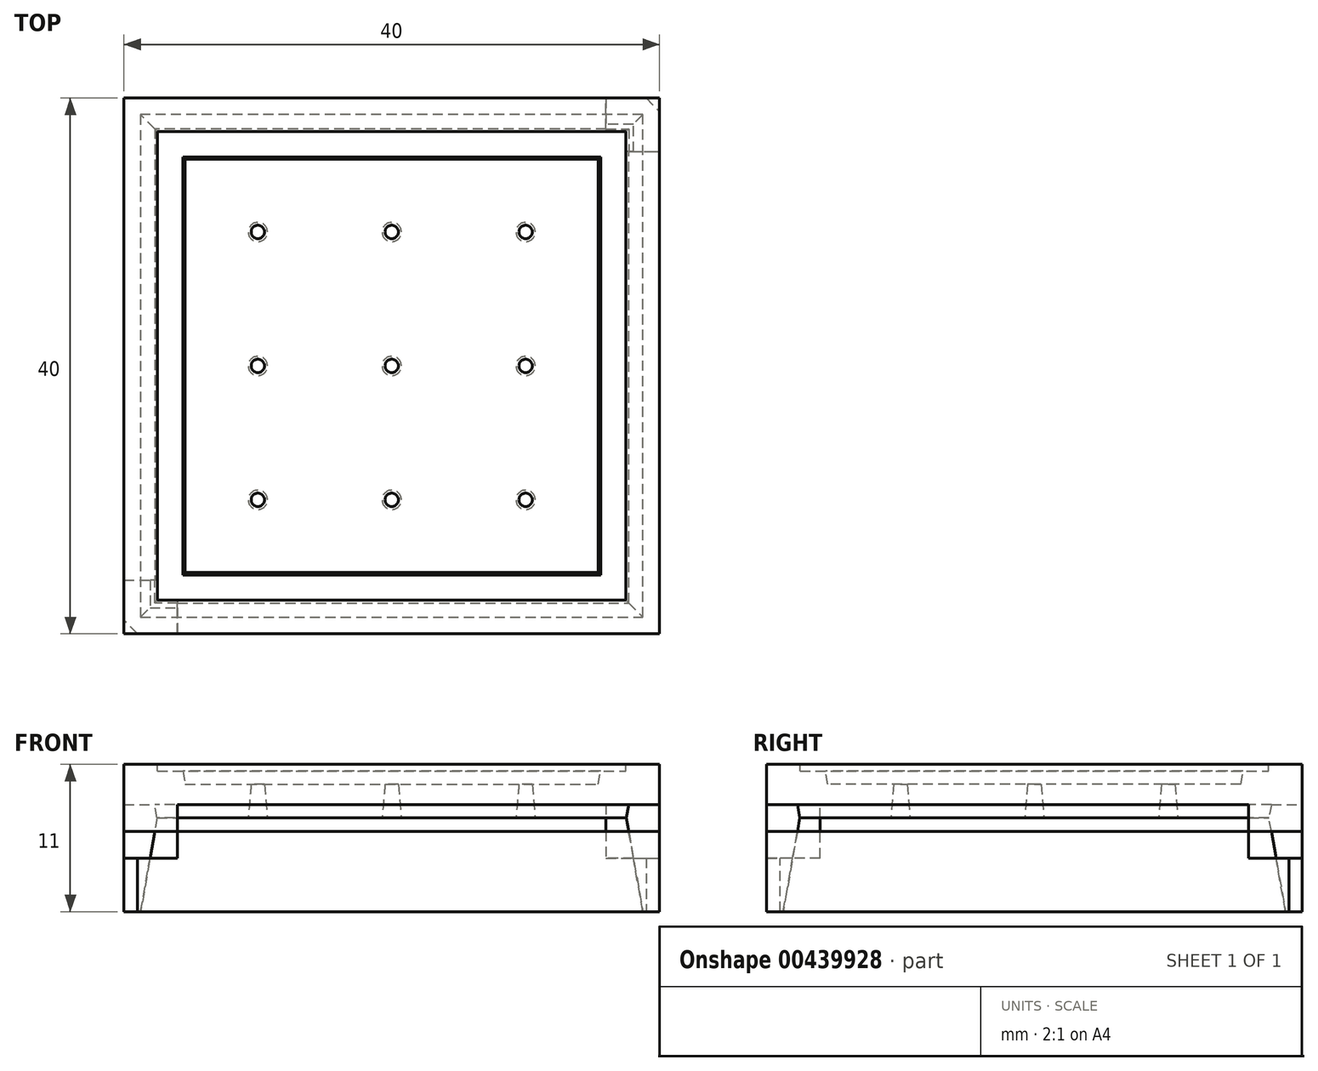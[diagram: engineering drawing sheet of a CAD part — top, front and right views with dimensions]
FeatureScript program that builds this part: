
annotation { "Feature Type Name" : "Feature", "Feature Type Description" : "" }
export const myFeature = defineFeature(function(context is Context, id is Id, definition is map)
    precondition{}
    {
        {
            var Q0;
            Q0=qCreatedBy(makeId("Top.planeOp"),FACE);
            var sketch = newSketch(context, id + "F0", { "sketchPlane" : qUnion([Q0])});
            skLineSegment(sketch, "E0.bottom", {"start": v(0, 0) * mm, "end": v(40, 0) * mm});
            skLineSegment(sketch, "E0.top", {"start": v(0, 40) * mm, "end": v(40, 40) * mm});
            skLineSegment(sketch, "E0.left", {"start": v(0, 0) * mm, "end": v(0, 40) * mm});
            skLineSegment(sketch, "E0.right", {"start": v(40, 0) * mm, "end": v(40, 40) * mm});
            skSolve(sketch);
        }
        {
            var Q0;
            Q0 = qSketchRegion(id + "F0", true);
            extrude(context, id + "F1", {"entities" : qUnion([Q0]), "depth" : 6 * mm});
        }
        {
            var Q0;
            Q0=makeQuery(id+"F1.opExtrude","CAP_FACE",FACE,{"disambiguationData":[OSD([sQuery(id+"F0.wireOp",EDGE,"E0.bottom"),sQuery(id+"F0.wireOp",EDGE,"E0.top"),sQuery(id+"F0.wireOp",EDGE,"E0.left"),sQuery(id+"F0.wireOp",EDGE,"E0.right")])],"isStart":false});
            var sketch = newSketch(context, id + "F2", { "sketchPlane" : qUnion([Q0])});
            skLineSegment(sketch, "E1.bottom", {"start": v(2.3, 2.3) * mm, "end": v(37.7, 2.3) * mm});
            skLineSegment(sketch, "E1.top", {"start": v(2.3, 37.7) * mm, "end": v(37.7, 37.7) * mm});
            skLineSegment(sketch, "E1.left", {"start": v(2.3, 2.3) * mm, "end": v(2.3, 37.7) * mm});
            skLineSegment(sketch, "E1.right", {"start": v(37.7, 2.3) * mm, "end": v(37.7, 37.7) * mm});
            skSolve(sketch);
        }
        {
            var Q0;
            Q0=makeQuery(id+"F1.opExtrude","CAP_FACE",FACE,{"disambiguationData":[OSD([sQuery(id+"F0.wireOp",EDGE,"E0.bottom"),sQuery(id+"F0.wireOp",EDGE,"E0.top"),sQuery(id+"F0.wireOp",EDGE,"E0.left"),sQuery(id+"F0.wireOp",EDGE,"E0.right")])],"isStart":false});
            cPlane(context, id + "F3", {"entities" : qUnion([Q0]), "cplaneType" : CPlaneType.OFFSET, "offset" : 5 * mm, "width" : 150 * mm, "height" : 150 * mm});
        }
        {
            var Q0;
            Q0=qCreatedBy(id+"F3.planeOp",FACE);
            var sketch = newSketch(context, id + "F4", { "sketchPlane" : qUnion([Q0])});
            skLineSegment(sketch, "E2.bottom", {"start": v(0, 0) * mm, "end": v(40, 0) * mm});
            skLineSegment(sketch, "E2.top", {"start": v(0, 40) * mm, "end": v(40, 40) * mm});
            skLineSegment(sketch, "E2.left", {"start": v(0, 0) * mm, "end": v(0, 40) * mm});
            skLineSegment(sketch, "E2.right", {"start": v(40, 0) * mm, "end": v(40, 40) * mm});
            skSolve(sketch);
        }
        {
            var Q0;
            Q0 = qSketchRegion(id + "F4", true);
            extrude(context, id + "F5", {"entities" : qUnion([Q0]), "oppositeDirection" : true, "depth" : 3 * mm});
        }
        {
            var Q0;
            Q0=makeQuery(id+"F2.imprint","IMPRINT",FACE,{"disambiguationData":[TD([[makeQuery(id+"F2.imprint","IMPRINT",EDGE,{"derivedFrom":sQuery(id+"F2.wireOp",EDGE,"E1.bottom")}),1.0]])]});
            extrude(context, id + "F6", {"entities" : qUnion([Q0]), "operationType" : NewBodyOperationType.REMOVE, "oppositeDirection" : true, "depth" : 4 * mm, "hasDraft" : true, "draftAngle" : 10 * degree, "draftPullDirection" : true});
        }
        {
            var Q0;
            Q0=qCreatedBy(id+"FNHtQi6ISW0JxXh_2.planeOp",FACE);
            var sketch = newSketch(context, id + "F7", { "sketchPlane" : qUnion([Q0])});
            skCircle(sketch, "E3", {"center": v(0, 3) * mm, "radius": 0.25 * mm});
            skSolve(sketch);
        }
        {
            var Q0;
            Q0=makeQuery(id+"F5.opExtrude","CAP_FACE",FACE,{"disambiguationData":[OSD([sQuery(id+"F4.wireOp",EDGE,"E2.bottom"),sQuery(id+"F4.wireOp",EDGE,"E2.top"),sQuery(id+"F4.wireOp",EDGE,"E2.left"),sQuery(id+"F4.wireOp",EDGE,"E2.right")])],"isStart":false});
            var sketch = newSketch(context, id + "F8", { "sketchPlane" : qUnion([Q0])});
            skLineSegment(sketch, "E4.bottom", {"start": v(2.3, -2.3) * mm, "end": v(37.7, -2.3) * mm});
            skLineSegment(sketch, "E4.top", {"start": v(2.3, -37.7) * mm, "end": v(37.7, -37.7) * mm});
            skLineSegment(sketch, "E4.left", {"start": v(2.3, -2.3) * mm, "end": v(2.3, -37.7) * mm});
            skLineSegment(sketch, "E4.right", {"start": v(37.7, -2.3) * mm, "end": v(37.7, -37.7) * mm});
            skSolve(sketch);
        }
        {
            var Q0;
            Q0=makeQuery(id+"F8.imprint","IMPRINT",FACE,{"disambiguationData":[TD([[makeQuery(id+"F8.imprint","IMPRINT",EDGE,{"derivedFrom":sQuery(id+"F8.wireOp",EDGE,"E4.bottom")}),-1.0]])]});
            extrude(context, id + "F9", {"entities" : qUnion([Q0]), "operationType" : NewBodyOperationType.ADD, "depth" : 1 * mm, "hasDraft" : true, "draftAngle" : 10 * degree, "draftPullDirection" : true});
        }
        {
            var Q0;
            Q0=makeQuery(id+"F5.opExtrude","CAP_FACE",FACE,{"disambiguationData":[OSD([sQuery(id+"F4.wireOp",EDGE,"E2.bottom"),sQuery(id+"F4.wireOp",EDGE,"E2.top"),sQuery(id+"F4.wireOp",EDGE,"E2.left"),sQuery(id+"F4.wireOp",EDGE,"E2.right")])],"isStart":true});
            shell(context, id + "F10", {"entities" : qUnion([Q0]), "thickness" : 2.5 * mm});
        }
        {
            var Q0;
            Q0=makeQuery(id+"F10.opShell","OFFSET_FACE",FACE,{"disambiguationData":[OSD([sQuery(id+"F8.wireOp",EDGE,"E4.bottom"),sQuery(id+"F8.wireOp",EDGE,"E4.top"),sQuery(id+"F8.wireOp",EDGE,"E4.left"),sQuery(id+"F8.wireOp",EDGE,"E4.right")])]});
            var sketch = newSketch(context, id + "F11", { "sketchPlane" : qUnion([Q0])});
            skCircle(sketch, "E5", {"center": v(10, 30) * mm, "radius": 0.5 * mm});
            skCircle(sketch, "E6.1.0.0", {"center": v(20, 30) * mm, "radius": 0.5 * mm});
            skCircle(sketch, "E6.2.0.0", {"center": v(30, 30) * mm, "radius": 0.5 * mm});
            skLineSegment(sketch, "E6.direction1", {"start": v(10, 30) * mm, "end": v(20, 30) * mm, "construction": true});
            skCircle(sketch, "E7.0.1.0", {"center": v(10, 20) * mm, "radius": 0.5 * mm});
            skCircle(sketch, "E7.0.2.0", {"center": v(10, 10) * mm, "radius": 0.5 * mm});
            skCircle(sketch, "E7.1.1.0", {"center": v(20, 20) * mm, "radius": 0.5 * mm});
            skCircle(sketch, "E7.1.2.0", {"center": v(20, 10) * mm, "radius": 0.5 * mm});
            skCircle(sketch, "E7.2.1.0", {"center": v(30, 20) * mm, "radius": 0.5 * mm});
            skCircle(sketch, "E7.2.2.0", {"center": v(30, 10) * mm, "radius": 0.5 * mm});
            skLineSegment(sketch, "E7.direction2", {"start": v(10, 30) * mm, "end": v(10, 20) * mm, "construction": true});
            skSolve(sketch);
        }
        {
            var Q0;
            Q0 = qSketchRegion(id + "F11", true);
            extrude(context, id + "F12", {"entities" : qUnion([Q0]), "operationType" : NewBodyOperationType.REMOVE, "endBound" : BoundingType.UP_TO_NEXT, "oppositeDirection" : true, "depth" : 25 * mm, "hasDraft" : true, "draftAngle" : 5 * degree});
        }
        {
            var Q0;
            Q0=makeQuery(id+"F1.opExtrude","SWEPT_EDGE",EDGE,{"disambiguationData":[OSD([sQuery(id+"F0.wireOp",EDGE,"E0.bottom"),sQuery(id+"F0.wireOp",EDGE,"E0.left")])]});
            var Q1;
            Q1=makeQuery(id+"F1.opExtrude","SWEPT_EDGE",EDGE,{"disambiguationData":[OSD([sQuery(id+"F0.wireOp",EDGE,"E0.top"),sQuery(id+"F0.wireOp",EDGE,"E0.right")])]});
            chamfer(context, id + "F13", {"entities" : qUnion([Q0, Q1]), "width" : 1 * mm});
        }
        {
            var Q0;
            Q0=makeQuery(id+"F1.opExtrude","CAP_FACE",FACE,{"disambiguationData":[OSD([sQuery(id+"F0.wireOp",EDGE,"E0.bottom"),sQuery(id+"F0.wireOp",EDGE,"E0.top"),sQuery(id+"F0.wireOp",EDGE,"E0.left"),sQuery(id+"F0.wireOp",EDGE,"E0.right")])],"isStart":false});
            var sketch = newSketch(context, id + "F14", { "sketchPlane" : qUnion([Q0])});
            skLineSegment(sketch, "E8.bottom", {"start": v(0, 4) * mm, "end": v(4, 4) * mm});
            skLineSegment(sketch, "E8.top", {"start": v(0, 0) * mm, "end": v(4, 0) * mm});
            skLineSegment(sketch, "E8.left", {"start": v(0, 4) * mm, "end": v(0, 0) * mm});
            skLineSegment(sketch, "E8.right", {"start": v(4, 4) * mm, "end": v(4, 0) * mm});
            skLineSegment(sketch, "E9.bottom", {"start": v(36, 40) * mm, "end": v(40, 40) * mm});
            skLineSegment(sketch, "E9.top", {"start": v(36, 36) * mm, "end": v(40, 36) * mm});
            skLineSegment(sketch, "E9.left", {"start": v(36, 40) * mm, "end": v(36, 36) * mm});
            skLineSegment(sketch, "E9.right", {"start": v(40, 40) * mm, "end": v(40, 36) * mm});
            skSolve(sketch);
        }
        {
            var Q0;
            Q0 = qSketchRegion(id + "F14", true);
            extrude(context, id + "F15", {"entities" : qUnion([Q0]), "operationType" : NewBodyOperationType.REMOVE, "oppositeDirection" : true, "depth" : 2 * mm});
        }
        {
            var Q0;
            Q0=makeQuery(id+"F5.opExtrude","CAP_FACE",FACE,{"disambiguationData":[OSD([sQuery(id+"F4.wireOp",EDGE,"E2.bottom"),sQuery(id+"F4.wireOp",EDGE,"E2.top"),sQuery(id+"F4.wireOp",EDGE,"E2.left"),sQuery(id+"F4.wireOp",EDGE,"E2.right")])],"isStart":false});
            var sketch = newSketch(context, id + "F16", { "sketchPlane" : qUnion([Q0])});
            skSolve(sketch);
        }
        {
            var Q0;
            Q0=makeQuery(id+"F16.imprint","IMPRINT",FACE,{"disambiguationData":[TD([[makeQuery(id+"F16.imprint","IMPRINT",EDGE,{"derivedFrom":makeQuery(id+"F5.opExtrude","CAP_EDGE",EDGE,{"disambiguationData":[OSD([sQuery(id+"F4.wireOp",EDGE,"E2.bottom")])],"isStart":false})}),-1.0]])]});
            var sketch = newSketch(context, id + "F17", { "sketchPlane" : qUnion([Q0])});
            skLineSegment(sketch, "E10.bottom", {"start": v(0, 0) * mm, "end": v(4, 0) * mm});
            skLineSegment(sketch, "E10.top", {"start": v(0, -4) * mm, "end": v(4, -4) * mm});
            skLineSegment(sketch, "E10.left", {"start": v(0, 0) * mm, "end": v(0, -4) * mm});
            skLineSegment(sketch, "E10.right", {"start": v(4, 0) * mm, "end": v(4, -4) * mm});
            skLineSegment(sketch, "E11.bottom", {"start": v(36, -36) * mm, "end": v(40, -36) * mm});
            skLineSegment(sketch, "E11.top", {"start": v(36, -40) * mm, "end": v(40, -40) * mm});
            skLineSegment(sketch, "E11.left", {"start": v(36, -36) * mm, "end": v(36, -40) * mm});
            skLineSegment(sketch, "E11.right", {"start": v(40, -36) * mm, "end": v(40, -40) * mm});
            skSolve(sketch);
        }
        {
            var Q0;
            Q0 = qSketchRegion(id + "F17", true);
            extrude(context, id + "F18", {"entities" : qUnion([Q0]), "operationType" : NewBodyOperationType.ADD, "depth" : 2 * mm});
        }
        {
            var Q0;
            Q0=makeQuery(id+"F9.opExtrude","CAP_FACE",FACE,{"disambiguationData":[OSD([sQuery(id+"F8.wireOp",EDGE,"E4.bottom"),sQuery(id+"F8.wireOp",EDGE,"E4.top"),sQuery(id+"F8.wireOp",EDGE,"E4.left"),sQuery(id+"F8.wireOp",EDGE,"E4.right")])],"isStart":false});
            var sketch = newSketch(context, id + "F19", { "sketchPlane" : qUnion([Q0])});
            skLineSegment(sketch, "E12.bottom", {"start": v(2.48, -37.52) * mm, "end": v(37.52, -37.52) * mm});
            skLineSegment(sketch, "E12.top", {"start": v(2.48, -2.48) * mm, "end": v(37.52, -2.48) * mm});
            skLineSegment(sketch, "E12.left", {"start": v(2.48, -37.52) * mm, "end": v(2.48, -2.48) * mm});
            skLineSegment(sketch, "E12.right", {"start": v(37.52, -37.52) * mm, "end": v(37.52, -2.48) * mm});
            skSolve(sketch);
        }
        {
            var Q0;
            Q0 = qSketchRegion(id + "F19", true);
            extrude(context, id + "F20", {"entities" : qUnion([Q0]), "operationType" : NewBodyOperationType.REMOVE, "depth" : 25 * mm, "hasDraft" : true, "draftAngle" : 10 * degree});
        }
    });
